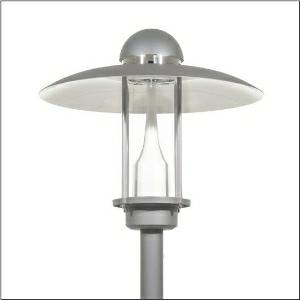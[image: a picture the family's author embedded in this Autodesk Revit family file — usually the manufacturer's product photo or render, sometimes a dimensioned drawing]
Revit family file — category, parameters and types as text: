
# Revit family: city-light_elegance_iq___st1_2a_5xa5265mf14hp_95af
name_source: partatom
category: Lighting Fixtures
units: mm (PartAtom-declared; Revit-internal decimal feet)

## family parameters
Cut with Voids When Loaded = No
Host = Face
Light Source = No
Part Type = Normal
Room Calculation Point = No
Round Connector Dimension = Use Diameter
Shared = No

## types (1)
- --- (1 x LED, 4050 lm, 33.6 W, 2700K)
    Apparent Load = 34 VA
    CIE Flux Codes = 22 61 93 98 100
    Color Rendering = 70
    Color Temperature = 2700K
    Default Elevation = 1800 mm
    Description = City-Light Elegance iQ, mast luminaire, Module 540 iQ-SR, primary light control with 3 zone facetted reflector, of plastic, silver coated, highly specular, structured, primary optical cover: cover, of PMMA, transparent, light distribution: ST1.2a, light emission: direct distribution, primary light characteristic: asymmetric, installation type: post-top, LED, High Power LED, rated luminous flux: 4.050lm, luminous efficacy: 121lm/W, light colour: 727, colour temperature: 2700K, control gear: iQ Street-Remote, control: pre-setting: logarithmic dimming characteristic, Street-Remote, Auto-Match, Temp-Guard, Lumen-Switch, Night-Set, Smart-Wire, Light-Fading, Desk-Remote (wireless, voltage-free reading and setting of iQ features in the workshop via application-optimized NFC function/RFID function), optimised constant luminous flux control (CLO 2.0), with terminal, 6-pole, max. 2.5mm², mains connection: 230..240V, AC, 50/60Hz, start of lifetime: 34W, end of service life: 36W, reduction: 15W, luminaire housing, upper part, of aluminium, coated, Siteco® metallic grey (DB 702S), diameter: 750mm, height: 675mm, spigot size: d x l = 76 x 70mm (post-top) | with reducer (optional accessory) 60 x 70mm, mounting height: 3..5m, post-top mast mounting element, of diecast aluminium, coated, Siteco® metallic grey (DB 702S), Module 540 iQ-SR, traffic white (RAL 9016), equipment: Power, protection rating (complete): IP65, insulation class (complete): insulation class II (safety insulation), certification: CE, ENEC, VDE, packaging unit: 1 piece

Light Distribution: ST1.2a
    Height = 675 mm
    Lamp = 1 x LED
    Lamp Light Flux = 4050 lm
    Lamp Power = 33.6 W
    Lamp count = 1
    Length = 750 mm
    Luminous efficacy = 121 lm/W
    Manufacturer = Siteco
    ModVariant = No
    Model = 5XA5265MF14HP
    Number of Poles = 1
    OnlyDefault = Yes
    Power Factor = 1
    Product Name = City-Light Elegance iQ | ST1.2a
    Product group = mast luminaire | pylon top
    ProductGroupID = 6100
    Protection Class = Protection class II
    Protection Degree = IP 65
    RLX_Detail_Level = 1
    RLX_Emergency_Light_Flux = 0 lm
    RLX_Emergency_Type = 0
    RLX_Emergency_Type_DB = No
    RlxData = <blob elided: 36589 chars, md5=1470bafc>
    Socket = socket
    Standby Power = 0 W
    System Light Flux = 4050 lm
    System Power = 34 W
    Type Comments = factory setting: luminous flux: 100 % | dim-lin: 254 | 695 mA
    Type Image = l_1006912.jpg
    URL = http://relux.com
    VarID = @adj_152618
    Voltage = 0 V
    Weight = 0.00 kg
    Width = 0 mm  [stored 0 ft]

note: [stored X ft] marks values corroborated as IEEE doubles in the binary element streams (Revit-internal decimal feet)

## geometry (parser evidence)
native form markers: Blend x4, Sweep x11
no freeform markers — native parametric forms only
